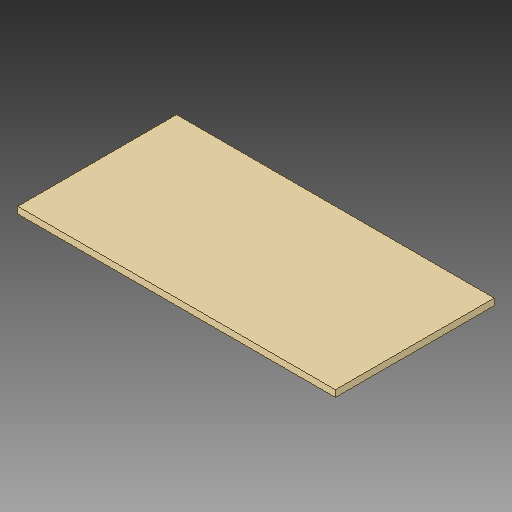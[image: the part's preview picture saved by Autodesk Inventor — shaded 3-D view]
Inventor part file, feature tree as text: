
AUTODESK INVENTOR PART (.ipt)
format: ipt  version: 2018 (Build 220112000, 112)  size: 77,824 bytes
history: native  units: in
note: dims shown in document units (in); Inventor stores cm internally (conversion verified against a paired STEP export)
features: other x3, sketch x1
ambient origin geometry x8: Origin, YZ Plane, XZ Plane, XY Plane, X Axis, Y Axis, Z Axis, Center Point
bodies: Solid1 (feature_tree)
feature tree (4):
  other  "Foor.ipt"
  other  "Solid1::Foor.ipt"
  other  "TaggingFeature1"
  sketch  "Sketch1"  dims[d0=0.3937in]
